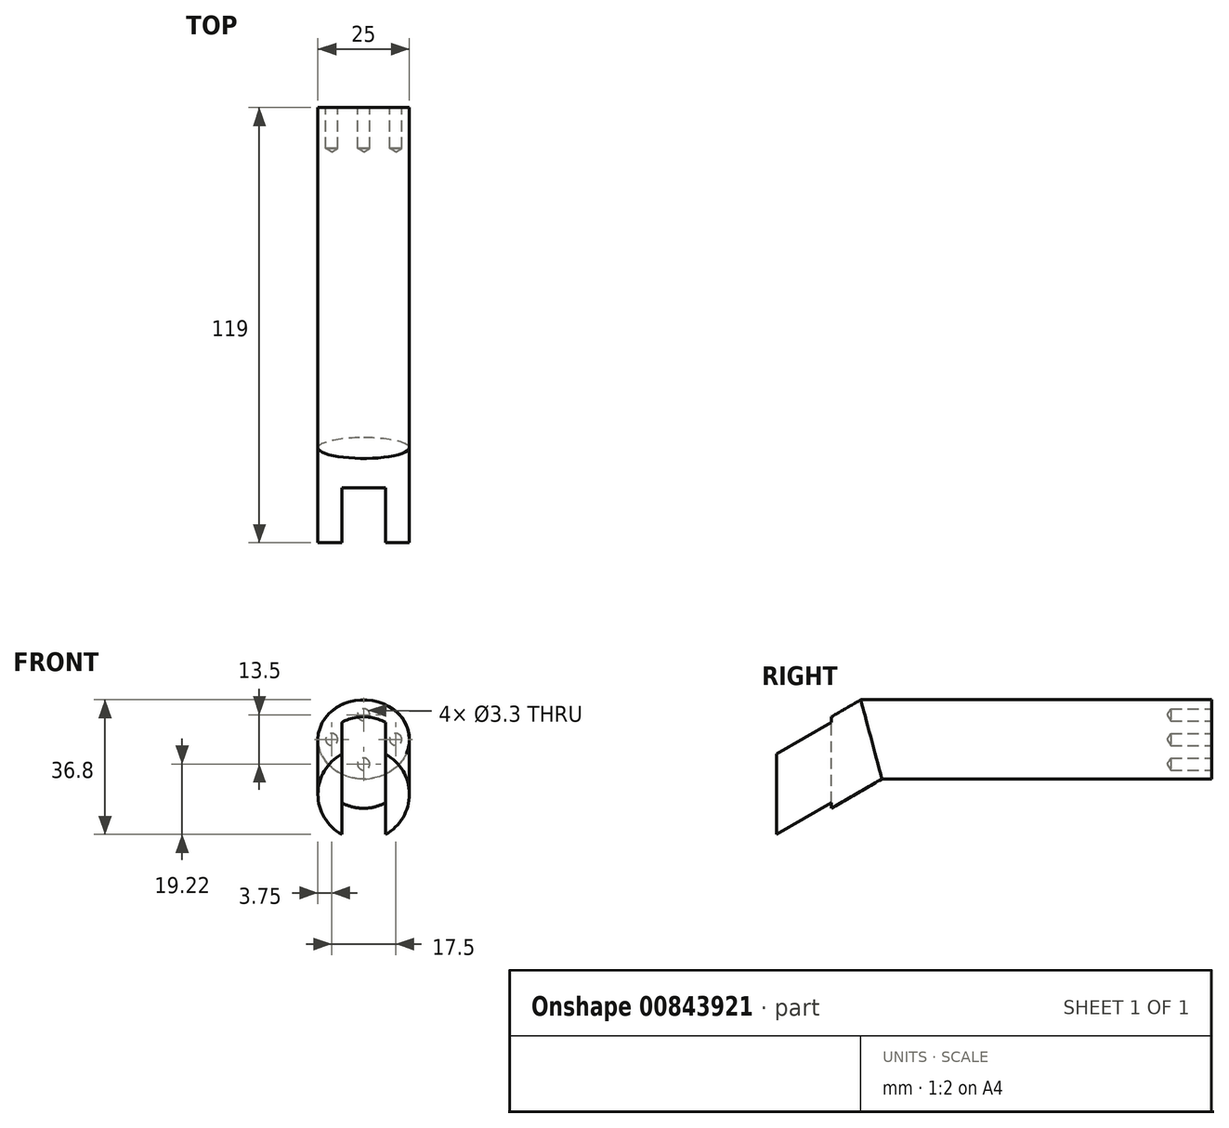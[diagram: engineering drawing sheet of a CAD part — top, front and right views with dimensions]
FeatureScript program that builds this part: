
annotation { "Feature Type Name" : "Feature", "Feature Type Description" : "" }
export const myFeature = defineFeature(function(context is Context, id is Id, definition is map)
    precondition{}
    {
        {
            var Q0;
            Q0=qCreatedBy(makeId("Front.planeOp"),FACE);
            var sketch = newSketch(context, id + "F0", { "sketchPlane" : qUnion([Q0])});
            skCircle(sketch, "E0", {"center": v(0, 0) * mm, "radius": 12.5 * mm});
            skSolve(sketch);
        }
        {
            var Q0;
            Q0=qCreatedBy(makeId("Right.planeOp"),FACE);
            var sketch = newSketch(context, id + "F1", { "sketchPlane" : qUnion([Q0])});
            skLineSegment(sketch, "E1", {"start": v(0, 0) * mm, "end": v(25.98, 15) * mm});
            skLineSegment(sketch, "E2", {"start": v(25.98, 15) * mm, "end": v(125.98, 15) * mm});
            skSolve(sketch);
        }
        {
            var Q0;
            Q0 = qSketchRegion(id + "F0", true);
            var Q1;
            Q1 = qConstructionFilter(qBodyType(qCreatedBy(id + "F1" ,EDGE), BodyType.WIRE), ConstructionObject.NO);
            sweep(context, id + "F2", {"profiles" : qUnion([Q0]), "path" : qUnion([Q1])});
        }
        {
            var Q0;
            Q0=qCreatedBy(makeId("Front.planeOp"),FACE);
            cPlane(context, id + "F3", {"entities" : qUnion([Q0]), "cplaneType" : CPlaneType.OFFSET, "offset" : 125 * mm, "oppositeDirection" : true, "width" : 150 * mm, "height" : 150 * mm});
        }
        {
            var Q0;
            Q0=qCreatedBy(id+"F3.planeOp",FACE);
            var sketch = newSketch(context, id + "F4", { "sketchPlane" : qUnion([Q0])});
            skCircle(sketch, "E3", {"center": v(0, 17) * mm, "radius": 20 * mm});
            skLineSegment(sketch, "E4", {"start": v(0, 0) * mm, "end": v(0, 17) * mm});
            skSolve(sketch);
        }
        {
            var Q0;
            Q0 = qSketchRegion(id + "F4", true);
            extrude(context, id + "F5", {"entities" : qUnion([Q0]), "operationType" : NewBodyOperationType.REMOVE, "depth" : 6 * mm, "offsetDistance" : 25 * mm, "hasSecondDirection" : true, "secondDirectionOppositeDirection" : true, "secondDirectionDepth" : 25 * mm});
        }
        {
            var Q0;
            Q0=makeQuery(id+"F5.boolean.opBoolean","COPY",FACE,{"derivedFrom":makeQuery(id+"F5.opExtrude","CAP_FACE",FACE,{"disambiguationData":[OSD([sQuery(id+"F4.wireOp",EDGE,"E3")])],"isStart":false})});
            var sketch = newSketch(context, id + "F6", { "sketchPlane" : qUnion([Q0])});
            skPoint(sketch, "E5", {"position": v(-8.75, 15) * mm});
            skPoint(sketch, "E6", {"position": v(0, 21.75) * mm});
            skPoint(sketch, "E7", {"position": v(8.75, 15) * mm});
            skPoint(sketch, "E8", {"position": v(0, 8.25) * mm});
            skLineSegment(sketch, "E9", {"start": v(0, 8.25) * mm, "end": v(0, 21.75) * mm, "construction": true});
            skLineSegment(sketch, "E10", {"start": v(-8.75, 15) * mm, "end": v(8.75, 15) * mm, "construction": true});
            skLineSegment(sketch, "E11", {"start": v(0, 0) * mm, "end": v(0, 15) * mm, "construction": true});
            skSolve(sketch);
        }
        {
            var Q0;
            Q0=sQuery(id+"F6.wireOp",VERTEX,"E6");
            var Q1;
            Q1=sQuery(id+"F6.wireOp",VERTEX,"E5");
            var Q2;
            Q2=sQuery(id+"F6.wireOp",VERTEX,"E8");
            var Q3;
            Q3=sQuery(id+"F6.wireOp",VERTEX,"E7");
            var Q4;
            Q4=makeQuery(id+"F2.opSweep","SWEPT_BODY",BODY,{"disambiguationData":[OSD([sQuery(id+"F0.wireOp",EDGE,"E0"),sQuery(id+"F1.wireOp",EDGE,"E2")])]});
            hole(context, id + "F7", {"style" : HoleStyle.SIMPLE, "endStyle" : HoleEndStyle.BLIND, "standardTappedOrClearance" : lookupTablePath({ "standard" : "ISO", "engagement" : "75%", "pitch" : "0.7 mm", "size" : "M4", "type" : "Tapped" }), "standardBlindInLast" : lookupTablePath({ "standard" : "ISO", "engagement" : "75%", "pitch" : "0.7 mm", "size" : "M4", "type" : "Tapped" }), "holeDiameter" : 3.3 * mm, "majorDiameter" : 4 * mm, "showTappedDepth" : true, "holeDepth" : 11.1 * mm, "tappedDepth" : 9 * mm, "tapClearance" : 3, "startFromSketch" : true, "locations" : qUnion([Q0, Q1, Q2, Q3]), "scope" : qUnion([Q4])});
        }
        {
            var Q0;
            Q0=makeQuery(id+"F2.opSweep","CAP_FACE",FACE,{"disambiguationData":[OSD([sQuery(id+"F0.wireOp",EDGE,"E0"),sQuery(id+"F1.wireOp",VERTEX,"E1.start")])],"isStart":true});
            var sketch = newSketch(context, id + "F8", { "sketchPlane" : qUnion([Q0])});
            skLineSegment(sketch, "E12.bottom", {"start": v(-6, -13) * mm, "end": v(6, -13) * mm});
            skLineSegment(sketch, "E12.top", {"start": v(-6, 17) * mm, "end": v(6, 17) * mm});
            skLineSegment(sketch, "E12.left", {"start": v(-6, -13) * mm, "end": v(-6, 17) * mm});
            skLineSegment(sketch, "E12.right", {"start": v(6, -13) * mm, "end": v(6, 17) * mm});
            skLineSegment(sketch, "E13", {"start": v(0, 0) * mm, "end": v(0, 17) * mm, "construction": true});
            skSolve(sketch);
        }
        {
            var Q0;
            Q0 = qSketchRegion(id + "F8", true);
            extrude(context, id + "F9", {"entities" : qUnion([Q0]), "operationType" : NewBodyOperationType.REMOVE, "oppositeDirection" : true, "depth" : 15 * mm, "offsetDistance" : 25 * mm});
        }
        {
            var Q0;
            Q0=makeQuery(id+"F9.boolean.opBoolean","COPY",FACE,{"derivedFrom":makeQuery(id+"F9.opExtrude","SWEPT_FACE",FACE,{"disambiguationData":[OSD([sQuery(id+"F8.wireOp",EDGE,"E12.top")])]})});
            var sketch = newSketch(context, id + "F10", { "sketchPlane" : qUnion([Q0])});
            skLineSegment(sketch, "E14", {"start": v(-6, -10.45) * mm, "end": v(-6, -15) * mm});
            skLineSegment(sketch, "E15", {"start": v(-6, -15) * mm, "end": v(6, -15) * mm});
            skLineSegment(sketch, "E16", {"start": v(6, -15) * mm, "end": v(6, -10.45) * mm});
            skLineSegment(sketch, "E17", {"start": v(-6, -10.45) * mm, "end": v(6, -10.45) * mm, "construction": true});
            skArc(sketch, "E18", {"start": v(6, -10.45) * mm, "mid": v(0, -7.74) * mm, "end": v(-6, -10.45) * mm});
            skSolve(sketch);
        }
        {
            var Q0;
            Q0 = qSketchRegion(id + "F10", true);
            extrude(context, id + "F11", {"entities" : qUnion([Q0]), "operationType" : NewBodyOperationType.REMOVE, "oppositeDirection" : true, "depth" : 25 * mm, "offsetDistance" : 25 * mm});
        }
    });
